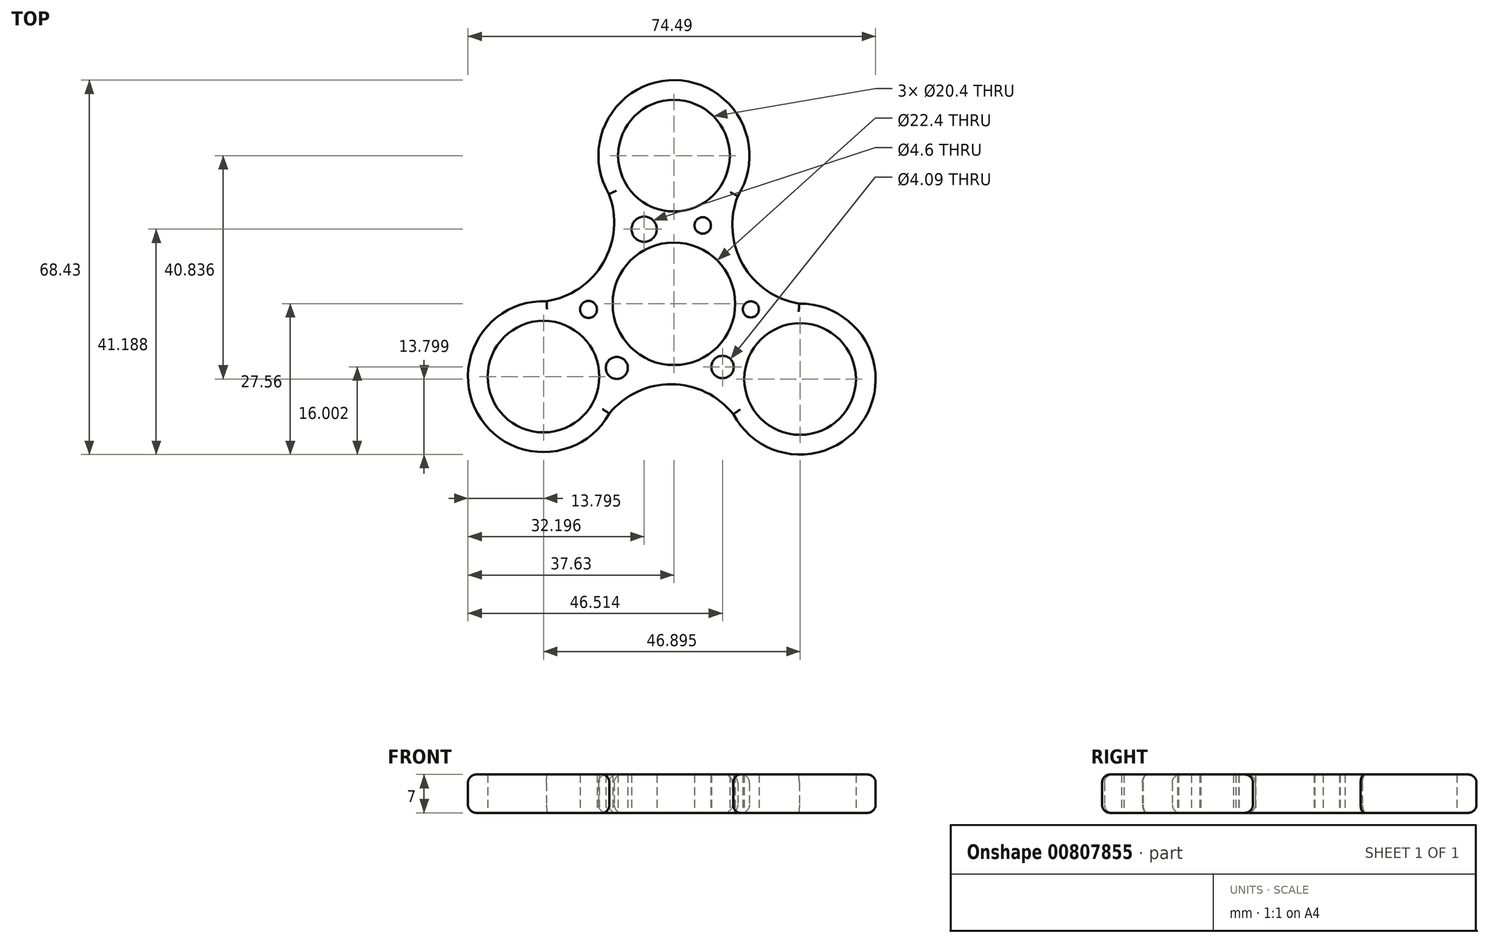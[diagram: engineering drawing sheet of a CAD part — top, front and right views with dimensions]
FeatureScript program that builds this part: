
annotation { "Feature Type Name" : "Feature", "Feature Type Description" : "" }
export const myFeature = defineFeature(function(context is Context, id is Id, definition is map)
    precondition{}
    {
        {
            var Q0;
            Q0=qCreatedBy(makeId("Top.planeOp"),FACE);
            var sketch = newSketch(context, id + "F0", { "sketchPlane" : qUnion([Q0])});
            skCircle(sketch, "E0", {"center": v(0, 0) * mm, "radius": 11.2 * mm});
            skCircle(sketch, "E1", {"center": v(0, 27.07) * mm, "radius": 10.2 * mm});
            skArc(sketch, "E2", {"start": v(11.66, 19.7) * mm, "mid": v(0.2, 40.87) * mm, "end": v(-11.87, 20.04) * mm});
            skArc(sketch, "E3.1.0", {"start": v(-23.27, 0.47) * mm, "mid": v(-35.89, -20.04) * mm, "end": v(-11.8, -20.08) * mm});
            skCircle(sketch, "E3.1.1", {"center": v(-23.83, -13.31) * mm, "radius": 10.2 * mm});
            skArc(sketch, "E3.2.0", {"start": v(10.84, -20.17) * mm, "mid": v(34.9, -20.84) * mm, "end": v(22.9, 0.04) * mm});
            skCircle(sketch, "E3.2.1", {"center": v(23.06, -13.76) * mm, "radius": 10.2 * mm});
            skPoint(sketch, "E3.center", {"position": v(-0.26, 0) * mm});
            skArc(sketch, "E4", {"start": v(12.88, 22.13) * mm, "mid": v(11.97, 8.4) * mm, "end": v(22.9, 0.04) * mm});
            skArc(sketch, "E5.1.0", {"start": v(-26, 0.32) * mm, "mid": v(-13.64, 6.39) * mm, "end": v(-11.87, 20.04) * mm});
            skArc(sketch, "E5.2.0", {"start": v(12.34, -22.45) * mm, "mid": v(0.9, -14.79) * mm, "end": v(-11.8, -20.08) * mm});
            skSolve(sketch);
        }
        {
            var Q0;
            Q0=qSketchRegion(id+"F0",true);
            extrude(context, id + "F1", {"entities" : qUnion([Q0]), "depth" : 7 * mm, "offsetDistance" : 25 * mm});
        }
        {
            var Q0;
            Q0=makeQuery(id+"F1.opExtrude","CAP_EDGE",EDGE,{"disambiguationData":[OSD([sQuery(id+"F0.wireOp",EDGE,"E2")])],"isStart":false});
            var Q1;
            Q1=makeQuery(id+"F1.opExtrude","CAP_EDGE",EDGE,{"disambiguationData":[OSD([sQuery(id+"F0.wireOp",EDGE,"E5.1.0")])],"isStart":false});
            var Q2;
            Q2=makeQuery(id+"F1.opExtrude","CAP_EDGE",EDGE,{"disambiguationData":[OSD([sQuery(id+"F0.wireOp",EDGE,"E3.1.0")])],"isStart":false});
            var Q3;
            Q3=makeQuery(id+"F1.opExtrude","CAP_EDGE",EDGE,{"disambiguationData":[OSD([sQuery(id+"F0.wireOp",EDGE,"E5.2.0")])],"isStart":false});
            var Q4;
            Q4=makeQuery(id+"F1.opExtrude","CAP_EDGE",EDGE,{"disambiguationData":[OSD([sQuery(id+"F0.wireOp",EDGE,"E3.2.0")])],"isStart":false});
            var Q5;
            Q5=makeQuery(id+"F1.opExtrude","CAP_EDGE",EDGE,{"disambiguationData":[OSD([sQuery(id+"F0.wireOp",EDGE,"E4")])],"isStart":false});
            var Q6;
            Q6=makeQuery(id+"F1.opExtrude","CAP_EDGE",EDGE,{"disambiguationData":[OSD([sQuery(id+"F0.wireOp",EDGE,"E2")])],"isStart":true});
            var Q7;
            Q7=makeQuery(id+"F1.opExtrude","CAP_EDGE",EDGE,{"disambiguationData":[OSD([sQuery(id+"F0.wireOp",EDGE,"E5.1.0")])],"isStart":true});
            var Q8;
            Q8=makeQuery(id+"F1.opExtrude","CAP_EDGE",EDGE,{"disambiguationData":[OSD([sQuery(id+"F0.wireOp",EDGE,"E3.1.0")])],"isStart":true});
            var Q9;
            Q9=makeQuery(id+"F1.opExtrude","CAP_EDGE",EDGE,{"disambiguationData":[OSD([sQuery(id+"F0.wireOp",EDGE,"E5.2.0")])],"isStart":true});
            var Q10;
            Q10=makeQuery(id+"F1.opExtrude","CAP_EDGE",EDGE,{"disambiguationData":[OSD([sQuery(id+"F0.wireOp",EDGE,"E3.2.0")])],"isStart":true});
            var Q11;
            Q11=makeQuery(id+"F1.opExtrude","CAP_EDGE",EDGE,{"disambiguationData":[OSD([sQuery(id+"F0.wireOp",EDGE,"E4")])],"isStart":true});
            fillet(context, id + "F2", {"entities" : qUnion([Q0, Q1, Q2, Q3, Q4, Q5, Q6, Q7, Q8, Q9, Q10, Q11]), "radius" : 1.5 * mm, "tangentPropagation" : true, "allowEdgeOverflow" : false});
        }
        {
            var Q0;
            Q0=makeQuery(id+"F1.opExtrude","CAP_FACE",FACE,{"disambiguationData":[OSD([sQuery(id+"F0.wireOp",EDGE,"E0"),sQuery(id+"F0.wireOp",EDGE,"E1"),sQuery(id+"F0.wireOp",EDGE,"E2"),sQuery(id+"F0.wireOp",EDGE,"E3.1.0"),sQuery(id+"F0.wireOp",EDGE,"E3.1.1"),sQuery(id+"F0.wireOp",EDGE,"E3.2.0"),sQuery(id+"F0.wireOp",EDGE,"E3.2.1"),sQuery(id+"F0.wireOp",EDGE,"E4"),sQuery(id+"F0.wireOp",EDGE,"E5.1.0"),sQuery(id+"F0.wireOp",EDGE,"E5.2.0")])],"isStart":true});
            var sketch = newSketch(context, id + "F3", { "sketchPlane" : qUnion([Q0])});
            skCircle(sketch, "E6", {"center": v(-10.26, 11.9) * mm, "radius": 1.54 * mm});
            skCircle(sketch, "E7", {"center": v(8.88, 11.56) * mm, "radius": 2.05 * mm});
            skCircle(sketch, "E8", {"center": v(14.06, 1.03) * mm, "radius": 1.47 * mm});
            skCircle(sketch, "E9", {"center": v(-15.61, 1.03) * mm, "radius": 1.55 * mm});
            skCircle(sketch, "E10", {"center": v(-5.43, -13.63) * mm, "radius": 2.3 * mm});
            skCircle(sketch, "E11", {"center": v(5.26, -14.32) * mm, "radius": 1.5 * mm});
            skSolve(sketch);
        }
        {
            var Q0;
            Q0=makeQuery(id+"F3.imprint","IMPRINT",FACE,{"disambiguationData":[TD([[makeQuery(id+"F3.imprint","IMPRINT",EDGE,{"derivedFrom":sQuery(id+"F3.wireOp",EDGE,"E7")}),1.0]])]});
            var Q1;
            Q1=makeQuery(id+"F3.imprint","IMPRINT",FACE,{"disambiguationData":[TD([[makeQuery(id+"F3.imprint","IMPRINT",EDGE,{"derivedFrom":sQuery(id+"F3.wireOp",EDGE,"E8")}),1.0]])]});
            var Q2;
            Q2=makeQuery(id+"F3.imprint","IMPRINT",FACE,{"disambiguationData":[TD([[makeQuery(id+"F3.imprint","IMPRINT",EDGE,{"derivedFrom":sQuery(id+"F3.wireOp",EDGE,"E9")}),1.0]])]});
            var Q3;
            Q3=makeQuery(id+"F3.imprint","IMPRINT",FACE,{"disambiguationData":[TD([[makeQuery(id+"F3.imprint","IMPRINT",EDGE,{"derivedFrom":sQuery(id+"F3.wireOp",EDGE,"E10")}),1.0]])]});
            var Q4;
            Q4=makeQuery(id+"F3.imprint","IMPRINT",FACE,{"disambiguationData":[TD([[makeQuery(id+"F3.imprint","IMPRINT",EDGE,{"derivedFrom":sQuery(id+"F3.wireOp",EDGE,"E11")}),1.0]])]});
            extrude(context, id + "F4", {"entities" : qUnion([Q0, Q1, Q2, Q3, Q4]), "operationType" : NewBodyOperationType.REMOVE, "oppositeDirection" : true, "depth" : 88888 * mm, "offsetDistance" : 25 * mm});
        }
        {
            var Q0;
            Q0=makeQuery(id+"F1.opExtrude","CAP_FACE",FACE,{"disambiguationData":[OSD([sQuery(id+"F0.wireOp",EDGE,"E0"),sQuery(id+"F0.wireOp",EDGE,"E1"),sQuery(id+"F0.wireOp",EDGE,"E2"),sQuery(id+"F0.wireOp",EDGE,"E3.1.0"),sQuery(id+"F0.wireOp",EDGE,"E3.1.1"),sQuery(id+"F0.wireOp",EDGE,"E3.2.0"),sQuery(id+"F0.wireOp",EDGE,"E3.2.1"),sQuery(id+"F0.wireOp",EDGE,"E4"),sQuery(id+"F0.wireOp",EDGE,"E5.1.0"),sQuery(id+"F0.wireOp",EDGE,"E5.2.0")])],"isStart":true});
            var sketch = newSketch(context, id + "F5", { "sketchPlane" : qUnion([Q0])});
            skCircle(sketch, "E12", {"center": v(-10.44, 11.73) * mm, "radius": 2.01 * mm});
            skSolve(sketch);
        }
        {
            var Q0;
            Q0=makeQuery(id+"F5.imprint","IMPRINT",FACE,{"disambiguationData":[TD([[makeQuery(id+"F5.imprint","IMPRINT",EDGE,{"derivedFrom":sQuery(id+"F5.wireOp",EDGE,"E12")}),1.0]])]});
            extrude(context, id + "F6", {"entities" : qUnion([Q0]), "operationType" : NewBodyOperationType.REMOVE, "oppositeDirection" : true, "depth" : 999 * mm, "offsetDistance" : 25 * mm});
        }
    });
